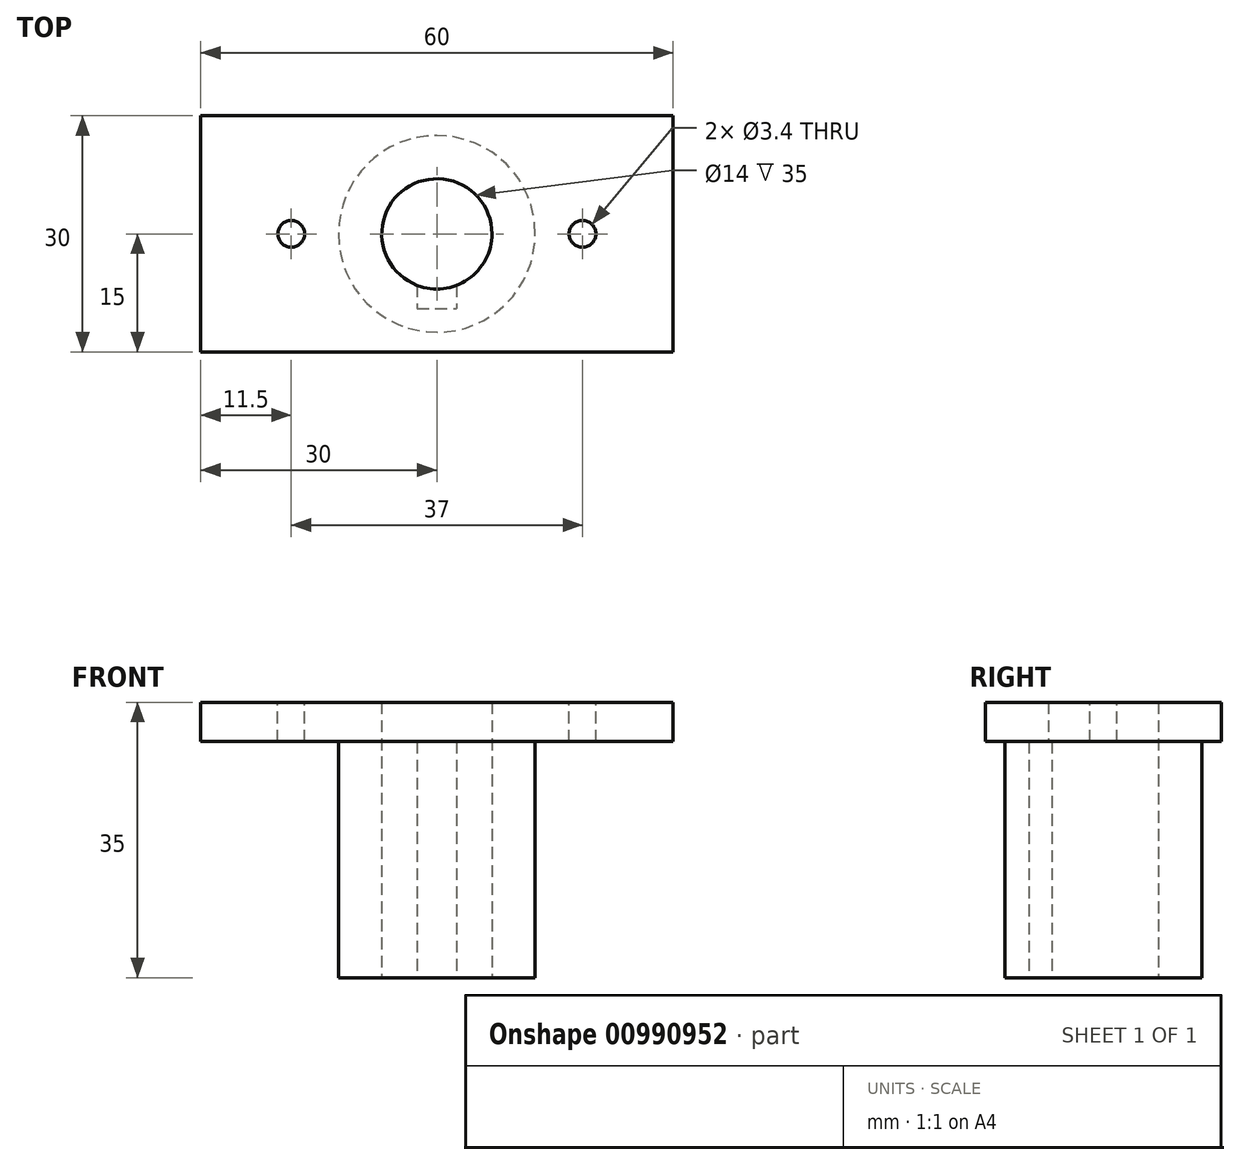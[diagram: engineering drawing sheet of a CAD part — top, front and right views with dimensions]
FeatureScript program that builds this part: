
annotation { "Feature Type Name" : "Feature", "Feature Type Description" : "" }
export const myFeature = defineFeature(function(context is Context, id is Id, definition is map)
    precondition{}
    {
        {
            var Q0;
            Q0=qCreatedBy(makeId("Top.planeOp"),FACE);
            var sketch = newSketch(context, id + "F0", { "sketchPlane" : qUnion([Q0])});
            skCircle(sketch, "E0", {"center": v(0, 0) * mm, "radius": 7 * mm});
            skLineSegment(sketch, "E1.bottom", {"start": v(30, -15) * mm, "end": v(-30, -15) * mm});
            skLineSegment(sketch, "E1.top", {"start": v(30, 15) * mm, "end": v(-30, 15) * mm});
            skLineSegment(sketch, "E1.left", {"start": v(30, -15) * mm, "end": v(30, 15) * mm});
            skLineSegment(sketch, "E1.right", {"start": v(-30, -15) * mm, "end": v(-30, 15) * mm});
            skLineSegment(sketch, "E2", {"start": v(0, 11.31) * mm, "end": v(0, -11.81) * mm, "construction": true});
            skLineSegment(sketch, "E3", {"start": v(-2.5, -6.54) * mm, "end": v(-2.5, -9.5) * mm});
            skLineSegment(sketch, "E4", {"start": v(-2.5, -9.5) * mm, "end": v(0, -9.5) * mm});
            skLineSegment(sketch, "E5.MirrorCS", {"start": v(2.5, -9.5) * mm, "end": v(0, -9.5) * mm});
            skLineSegment(sketch, "E6.MirrorCS", {"start": v(2.5, -6.54) * mm, "end": v(2.5, -9.5) * mm});
            skPoint(sketch, "E7", {"position": v(0, -7) * mm});
            skPoint(sketch, "E8", {"position": v(-18.5, 0) * mm});
            skPoint(sketch, "E9.MirrorP", {"position": v(18.5, 0) * mm});
            skSolve(sketch);
        }
        {
            var Q0;
            Q0=makeQuery(id+"F0.imprint","IMPRINT",FACE,{"disambiguationData":[TD([[makeQuery(id+"F0.imprint","IMPRINT",EDGE,{"derivedFrom":sQuery(id+"F0.wireOp",EDGE,"E1.bottom")}),-1.0]])]});
            var Q1;
            {var subQ0=sQuery(id+"F0.wireOp",EDGE,"E0");var subQ2=makeQuery(id+"F0.imprint","IMPRINT",VERTEX,{"derivedFrom":subQ0});Q1=makeQuery(id+"F0.imprint","IMPRINT",FACE,{"disambiguationData":[TD([[makeQuery(id+"F0.imprint","IMPRINT",EDGE,{"disambiguationData":[TD([[subQ2,-1.0]])],"derivedFrom":subQ0}),1.0]])]});}
            var Q2;
            {var subQ0=sQuery(id+"F0.wireOp",EDGE,"E3");Q2=makeQuery(id+"F0.imprint","IMPRINT",FACE,{"disambiguationData":[TD([[makeQuery(id+"F0.imprint","IMPRINT",EDGE,{"derivedFrom":subQ0}),1.0]])]});}
            extrude(context, id + "F1", {"entities" : qUnion([Q0, Q1, Q2]), "depth" : 35 * mm, "offsetDistance" : 25 * mm});
        }
        {
            var Q0;
            {var subQ0=sQuery(id+"F0.wireOp",EDGE,"E0");var subQ2=makeQuery(id+"F0.imprint","IMPRINT",VERTEX,{"derivedFrom":subQ0});Q0=makeQuery(id+"F0.imprint","IMPRINT",FACE,{"disambiguationData":[TD([[makeQuery(id+"F0.imprint","IMPRINT",EDGE,{"disambiguationData":[TD([[subQ2,-1.0]])],"derivedFrom":subQ0}),1.0]])]});}
            var Q1;
            {var subQ0=sQuery(id+"F0.wireOp",EDGE,"E3");Q1=makeQuery(id+"F0.imprint","IMPRINT",FACE,{"disambiguationData":[TD([[makeQuery(id+"F0.imprint","IMPRINT",EDGE,{"derivedFrom":subQ0}),1.0]])]});}
            extrude(context, id + "F2", {"entities" : qUnion([Q0, Q1]), "operationType" : NewBodyOperationType.REMOVE, "depth" : 30 * mm, "offsetDistance" : 25 * mm});
        }
        {
            var Q0;
            Q0=makeQuery(id+"F1.opExtrude","CAP_FACE",FACE,{"disambiguationData":[OSD([sQuery(id+"F0.wireOp",EDGE,"E1.bottom"),sQuery(id+"F0.wireOp",EDGE,"E1.top"),sQuery(id+"F0.wireOp",EDGE,"E1.left"),sQuery(id+"F0.wireOp",EDGE,"E1.right")])],"isStart":false});
            var sketch = newSketch(context, id + "F3", { "sketchPlane" : qUnion([Q0])});
            skCircle(sketch, "E10", {"center": v(0, 0) * mm, "radius": 2.5 * mm});
            skSolve(sketch);
        }
        {
            var Q0;
            Q0=makeQuery(id+"F0.imprint","IMPRINT",FACE,{"disambiguationData":[TD([[makeQuery(id+"F0.imprint","IMPRINT",EDGE,{"derivedFrom":sQuery(id+"F0.wireOp",EDGE,"E1.bottom")}),-1.0]])]});
            var sketch = newSketch(context, id + "F4", { "sketchPlane" : qUnion([Q0])});
            skCircle(sketch, "E11", {"center": v(0, 0) * mm, "radius": 12.5 * mm});
            skSolve(sketch);
        }
        {
            var Q0;
            Q0=makeQuery(id+"F4.imprint","IMPRINT",FACE,{"disambiguationData":[TD([[makeQuery(id+"F4.imprint","IMPRINT",EDGE,{"derivedFrom":sQuery(id+"F4.wireOp",EDGE,"E11")}),-1.0]])]});
            extrude(context, id + "F5", {"entities" : qUnion([Q0]), "operationType" : NewBodyOperationType.REMOVE, "depth" : 30 * mm, "offsetDistance" : 25 * mm});
        }
        {
            var Q0;
            Q0=makeQuery(id+"F3.imprint","IMPRINT",FACE,{"disambiguationData":[TD([[makeQuery(id+"F3.imprint","IMPRINT",EDGE,{"derivedFrom":sQuery(id+"F3.wireOp",EDGE,"E10")}),-1.0]])]});
            var sketch = newSketch(context, id + "F6", { "sketchPlane" : qUnion([Q0])});
            skCircle(sketch, "E12", {"center": v(-18.5, 0) * mm, "radius": 1.5 * mm});
            skCircle(sketch, "E13.MirrorC", {"center": v(18.5, 0) * mm, "radius": 1.5 * mm});
            skSolve(sketch);
        }
        {
            var Q0;
            Q0=sQuery(id+"F6.wireOp",VERTEX,"E12.center");
            var Q1;
            Q1=sQuery(id+"F6.wireOp",VERTEX,"E13.MirrorC.center");
            var Q2;
            Q2=makeQuery(id+"F1.opExtrude","SWEPT_BODY",BODY,{"disambiguationData":[OSD([sQuery(id+"F0.wireOp",EDGE,"E1.bottom"),sQuery(id+"F0.wireOp",EDGE,"E1.top"),sQuery(id+"F0.wireOp",EDGE,"E1.left"),sQuery(id+"F0.wireOp",EDGE,"E1.right")])]});
            hole(context, id + "F7", {"style" : HoleStyle.SIMPLE, "endStyle" : HoleEndStyle.THROUGH, "standardTappedOrClearance" : lookupTablePath({ "fit" : "Normal", "standard" : "ISO", "size" : "M3", "type" : "Clearance" }), "standardBlindInLast" : lookupTablePath({ "fit" : "Normal", "standard" : "ISO", "engagement" : "75%", "pitch" : "0.5 mm", "size" : "M3", "type" : "Clearance & tapped" }), "holeDiameter" : 3.4 * mm, "majorDiameter" : 5 * mm, "isTappedThrough" : true, "tappedDepth" : 12 * mm, "tapClearance" : 3, "locations" : qUnion([Q0, Q1]), "scope" : qUnion([Q2])});
        }
        {
            var Q0;
            Q0=sQuery(id+"F0.wireOp",VERTEX,"E0.center");
            var Q1;
            Q1=makeQuery(id+"F1.opExtrude","SWEPT_BODY",BODY,{"disambiguationData":[OSD([sQuery(id+"F0.wireOp",EDGE,"E1.bottom"),sQuery(id+"F0.wireOp",EDGE,"E1.top"),sQuery(id+"F0.wireOp",EDGE,"E1.left"),sQuery(id+"F0.wireOp",EDGE,"E1.right")])]});
            hole(context, id + "F8", {"style" : HoleStyle.SIMPLE, "endStyle" : HoleEndStyle.THROUGH, "oppositeDirection" : true, "standardTappedOrClearance" : lookupTablePath({ "fit" : "Normal", "standard" : "ISO", "size" : "M5", "type" : "Clearance" }), "standardBlindInLast" : lookupTablePath({ "fit" : "Normal", "standard" : "ISO", "engagement" : "75%", "pitch" : "0.8 mm", "size" : "M5", "type" : "Clearance & tapped" }), "holeDiameter" : 5.5 * mm, "majorDiameter" : 5 * mm, "isTappedThrough" : true, "tappedDepth" : 12 * mm, "tapClearance" : 3, "locations" : qUnion([Q0]), "scope" : qUnion([Q1])});
        }
    });
